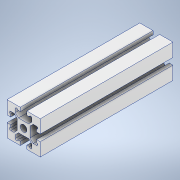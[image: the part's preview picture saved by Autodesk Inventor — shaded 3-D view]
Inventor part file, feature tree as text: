
AUTODESK INVENTOR PART (.ipt)
format: ipt  version: 2021 (Build 250183000, 183)  size: 167,936 bytes
history: native  units: in
note: dims shown in document units (in); Inventor stores cm internally (conversion verified against a paired STEP export)
features: other x2, thread x1
ambient origin geometry x8: Origin, YZ Plane, XZ Plane, XY Plane, X Axis, Y Axis, Z Axis, Center Point
bodies: Body1 (feature_tree)
feature tree (3):
  other  "Sólido1"
  thread  "Rosca1"  [1 undecoded]
  other  "Sólido2"
note: 1 required parameter value undecoded (feature->parameter linkage not recoverable at this tier; creation-order binding heuristic only, values carry confidence <= 0.55)
